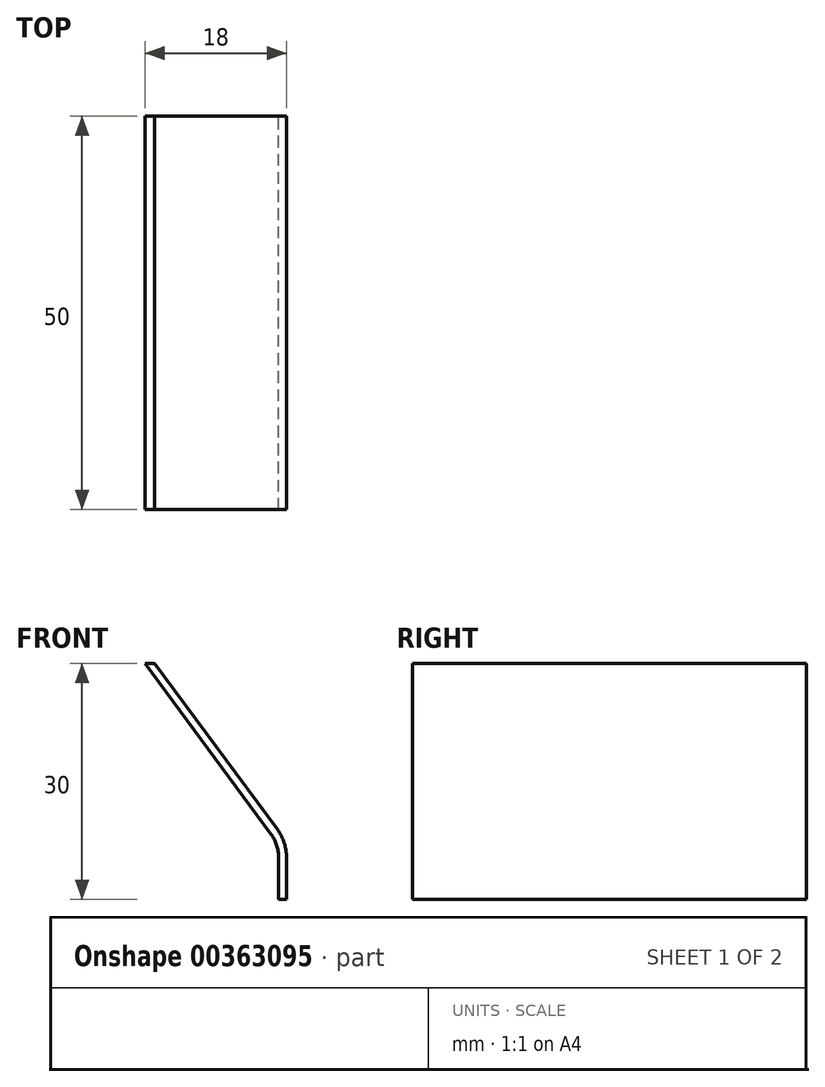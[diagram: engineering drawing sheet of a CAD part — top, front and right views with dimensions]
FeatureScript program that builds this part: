
annotation { "Feature Type Name" : "Feature", "Feature Type Description" : "" }
export const myFeature = defineFeature(function(context is Context, id is Id, definition is map)
    precondition{}
    {
        {
            var Q0;
            Q0=qCreatedBy(makeId("Front.planeOp"),FACE);
            var sketch = newSketch(context, id + "F0", { "sketchPlane" : qUnion([Q0])});
            skLineSegment(sketch, "E0.bottom", {"start": v(-9.24, 29.96) * mm, "end": v(-10.24, 29.96) * mm});
            skLineSegment(sketch, "E0.top", {"start": v(-26, 59.96) * mm, "end": v(-27.24, 59.96) * mm});
            skLineSegment(sketch, "E0.left", {"start": v(-9.24, 29.96) * mm, "end": v(-9.24, 35.26) * mm});
            skPoint(sketch, "E0.middle", {"position": v(-18.24, 44.96) * mm});
            skLineSegment(sketch, "E1", {"start": v(-10.24, 29.96) * mm, "end": v(-10.24, 35.26) * mm});
            skLineSegment(sketch, "E2", {"start": v(-11.22, 38.23) * mm, "end": v(-27.24, 59.96) * mm});
            skPoint(sketch, "E3.visualSharp", {"position": v(-10.24, 36.9) * mm});
            skArc(sketch, "E3.filletArc", {"start": v(-10.24, 35.26) * mm, "mid": v(-10.5, 36.83) * mm, "end": v(-11.22, 38.23) * mm});
            skLineSegment(sketch, "E4.0", {"start": v(-10.41, 38.82) * mm, "end": v(-26, 59.96) * mm});
            skArc(sketch, "E4.1", {"start": v(-9.24, 35.26) * mm, "mid": v(-9.54, 37.14) * mm, "end": v(-10.41, 38.82) * mm});
            skSolve(sketch);
        }
        {
            var Q0;
            Q0 = qSketchRegion(id + "F0", true);
            extrude(context, id + "F1", {"entities" : qUnion([Q0]), "depth" : 50 * mm});
        }
    });
